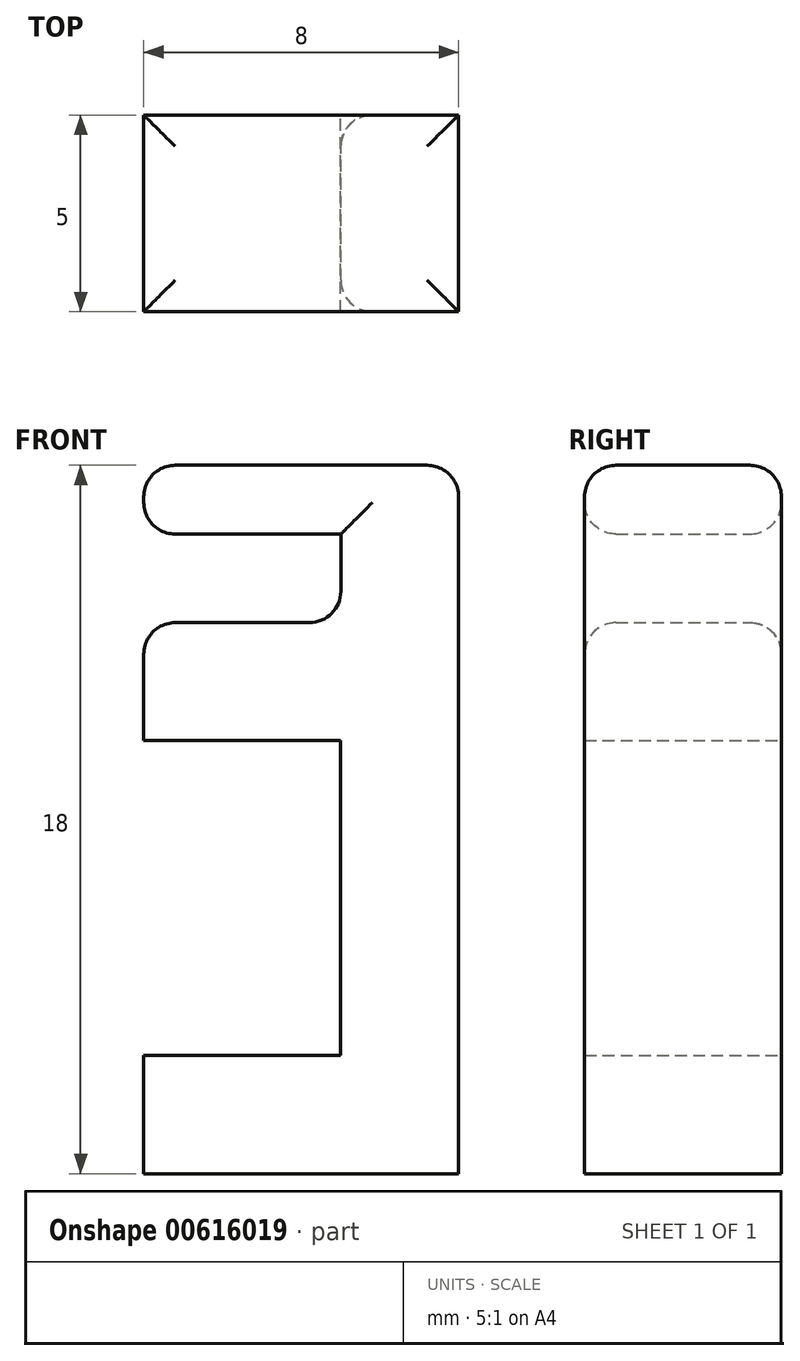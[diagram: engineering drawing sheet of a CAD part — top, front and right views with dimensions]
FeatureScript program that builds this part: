
annotation { "Feature Type Name" : "Feature", "Feature Type Description" : "" }
export const myFeature = defineFeature(function(context is Context, id is Id, definition is map)
    precondition{}
    {
        {
            var Q0;
            Q0=qCreatedBy(makeId("Front.planeOp"),FACE);
            var sketch = newSketch(context, id + "F0", { "sketchPlane" : qUnion([Q0])});
            skLineSegment(sketch, "E0", {"start": v(0, 0) * mm, "end": v(8, 0) * mm});
            skLineSegment(sketch, "E1", {"start": v(8, 0) * mm, "end": v(8, 18) * mm});
            skLineSegment(sketch, "E2", {"start": v(8, 18) * mm, "end": v(0, 18) * mm});
            skLineSegment(sketch, "E3", {"start": v(0, 18) * mm, "end": v(0, 16.25) * mm});
            skLineSegment(sketch, "E4", {"start": v(0, 16.25) * mm, "end": v(5, 16.25) * mm});
            skLineSegment(sketch, "E5", {"start": v(5, 16.25) * mm, "end": v(5, 14) * mm});
            skLineSegment(sketch, "E6", {"start": v(5, 14) * mm, "end": v(0, 14) * mm});
            skLineSegment(sketch, "E7", {"start": v(0, 14) * mm, "end": v(0, 11) * mm});
            skLineSegment(sketch, "E8", {"start": v(0, 11) * mm, "end": v(5, 11) * mm});
            skLineSegment(sketch, "E9", {"start": v(5, 11) * mm, "end": v(5, 3) * mm});
            skLineSegment(sketch, "E10", {"start": v(5, 3) * mm, "end": v(0, 3) * mm});
            skLineSegment(sketch, "E11", {"start": v(0, 3) * mm, "end": v(0, 0) * mm});
            skSolve(sketch);
        }
        {
            var Q0;
            Q0=makeQuery(id+"F0.imprint","IMPRINT",FACE,{"disambiguationData":[TD([[makeQuery(id+"F0.imprint","IMPRINT",EDGE,{"derivedFrom":sQuery(id+"F0.wireOp",EDGE,"E0")}),1.0]])]});
            extrude(context, id + "F1", {"entities" : qUnion([Q0]), "depth" : 5 * mm, "offsetDistance" : 25 * mm});
        }
        {
            var Q0;
            Q0=makeQuery(id+"F1.opExtrude","SWEPT_EDGE",EDGE,{"disambiguationData":[OSD([sQuery(id+"F0.wireOp",EDGE,"E2"),sQuery(id+"F0.wireOp",EDGE,"E3")])]});
            var Q1;
            Q1=makeQuery(id+"F1.opExtrude","SWEPT_EDGE",EDGE,{"disambiguationData":[OSD([sQuery(id+"F0.wireOp",EDGE,"E3"),sQuery(id+"F0.wireOp",EDGE,"E4")])]});
            var Q2;
            Q2=makeQuery(id+"F1.opExtrude","CAP_EDGE",EDGE,{"disambiguationData":[OSD([sQuery(id+"F0.wireOp",EDGE,"E6")])],"isStart":false});
            var Q3;
            Q3=makeQuery(id+"F1.opExtrude","CAP_EDGE",EDGE,{"disambiguationData":[OSD([sQuery(id+"F0.wireOp",EDGE,"E5")])],"isStart":false});
            var Q4;
            Q4=makeQuery(id+"F1.opExtrude","CAP_EDGE",EDGE,{"disambiguationData":[OSD([sQuery(id+"F0.wireOp",EDGE,"E5")])],"isStart":true});
            var Q5;
            Q5=makeQuery(id+"F1.opExtrude","CAP_EDGE",EDGE,{"disambiguationData":[OSD([sQuery(id+"F0.wireOp",EDGE,"E4")])],"isStart":false});
            var Q6;
            Q6=makeQuery(id+"F1.opExtrude","CAP_EDGE",EDGE,{"disambiguationData":[OSD([sQuery(id+"F0.wireOp",EDGE,"E6")])],"isStart":true});
            var Q7;
            Q7=makeQuery(id+"F1.opExtrude","SWEPT_EDGE",EDGE,{"disambiguationData":[OSD([sQuery(id+"F0.wireOp",EDGE,"E6"),sQuery(id+"F0.wireOp",EDGE,"OXqpamiX-PpRR-JcQ7-yJoM-eccZ9TBsgpAZ")])]});
            var Q8;
            Q8=makeQuery(id+"F1.opExtrude","CAP_EDGE",EDGE,{"disambiguationData":[OSD([sQuery(id+"F0.wireOp",EDGE,"E4")])],"isStart":true});
            var Q9;
            Q9=makeQuery(id+"F1.opExtrude","CAP_EDGE",EDGE,{"disambiguationData":[OSD([sQuery(id+"F0.wireOp",EDGE,"E2")])],"isStart":true});
            var Q10;
            Q10=makeQuery(id+"F1.opExtrude","CAP_EDGE",EDGE,{"disambiguationData":[OSD([sQuery(id+"F0.wireOp",EDGE,"E2")])],"isStart":false});
            var Q11;
            Q11=makeQuery(id+"F1.opExtrude","SWEPT_EDGE",EDGE,{"disambiguationData":[OSD([sQuery(id+"F0.wireOp",EDGE,"E1"),sQuery(id+"F0.wireOp",EDGE,"E2")])]});
            fillet(context, id + "F2", {"entities" : qUnion([Q0, Q1, Q2, Q3, Q4, Q5, Q6, Q7, Q8, Q9, Q10, Q11]), "radius" : 0.8 * mm, "tangentPropagation" : true, "allowEdgeOverflow" : false});
        }
    });
